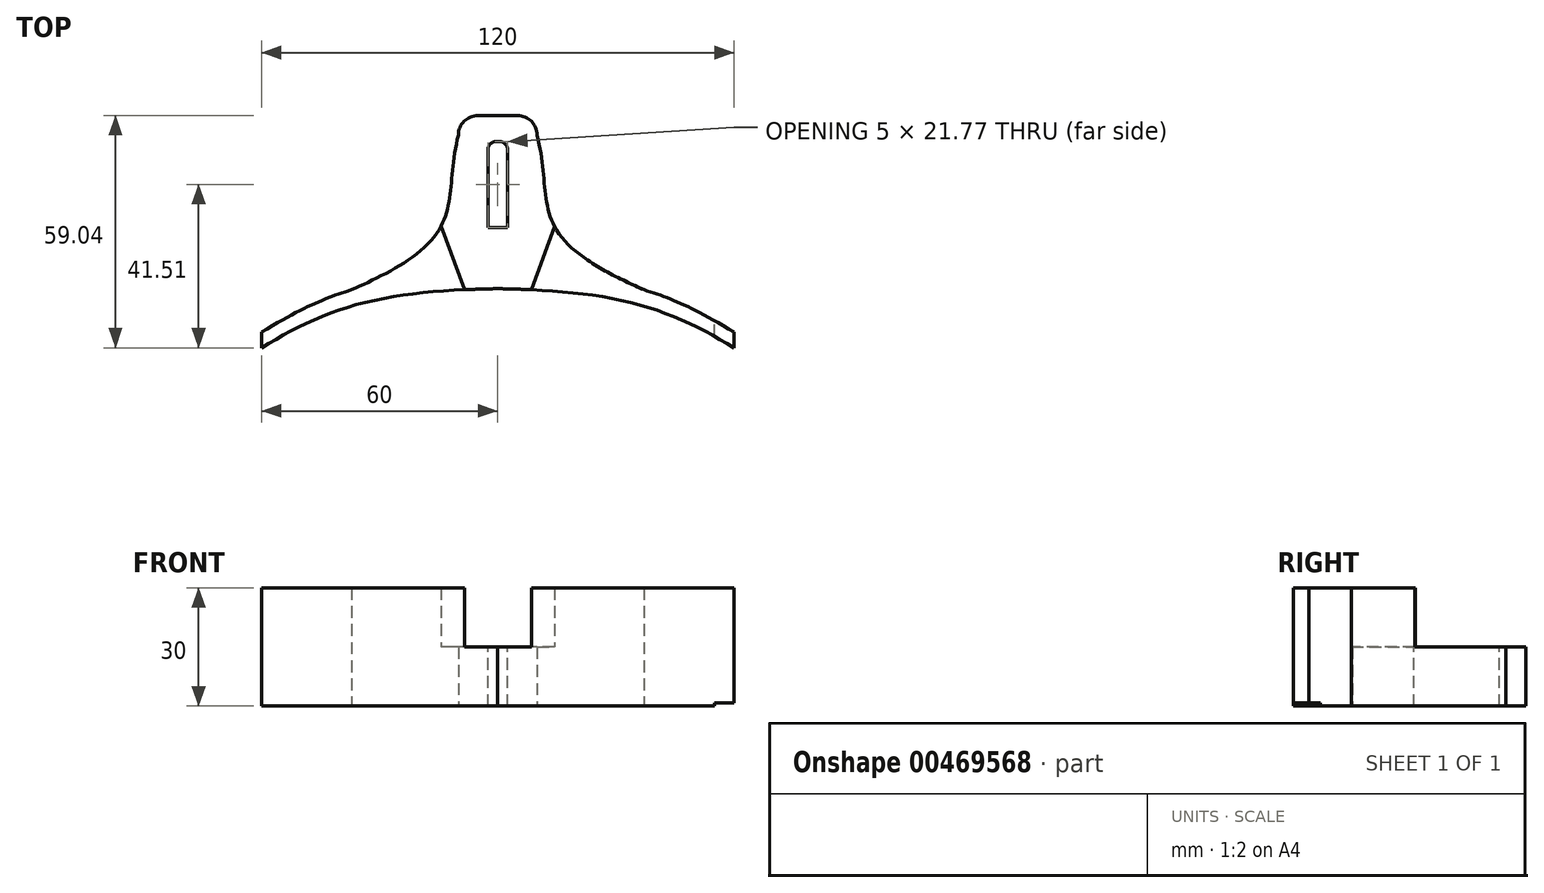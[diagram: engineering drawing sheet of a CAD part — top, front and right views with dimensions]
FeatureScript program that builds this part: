
annotation { "Feature Type Name" : "Feature", "Feature Type Description" : "" }
export const myFeature = defineFeature(function(context is Context, id is Id, definition is map)
    precondition{}
    {
        {
            var Q0;
            Q0=qCreatedBy(makeId("Top.planeOp"),FACE);
            var sketch = newSketch(context, id + "F0", { "sketchPlane" : qUnion([Q0])});
            skFitSpline(sketch, "E0", {"points": [v(10, 0) * mm, v(37.1, -4.27) * mm, v(60, -15.04) * mm], "startDerivative": vector(66.42, 0) * mm, "endDerivative": vector(68.25, -40.78) * mm});
            skLineSegment(sketch, "E1", {"start": v(5, 40) * mm, "end": v(0, 40) * mm});
            skPoint(sketch, "E2.visualSharp", {"position": v(10, 40) * mm});
            skArc(sketch, "E2.filletArc", {"start": v(10, 35) * mm, "mid": v(8.54, 38.54) * mm, "end": v(5, 40) * mm});
            skLineSegment(sketch, "E3", {"start": v(60, -15.04) * mm, "end": v(60, -19.04) * mm});
            skFitSpline(sketch, "E4", {"points": [v(60, -19.04) * mm, v(35.82, -8.06) * mm, v(0, -4) * mm], "startDerivative": vector(-46.55, 29) * mm, "endDerivative": vector(-72.62, 1.28) * mm});
            skFitSpline(sketch, "E5", {"points": [v(10, 35) * mm, v(15.27, 10.37) * mm, v(37.1, -4.27) * mm], "startDerivative": vector(15.22, -59.07) * mm, "endDerivative": vector(39.97, -17.86) * mm});
            skLineSegment(sketch, "E6.MirrorCS", {"start": v(-5, 40) * mm, "end": v(0, 40) * mm});
            skLineSegment(sketch, "E7.MirrorCS", {"start": v(-60, -15.04) * mm, "end": v(-60, -19.04) * mm});
            skArc(sketch, "E8.MirrorCS", {"start": v(-10, 35) * mm, "mid": v(-8.54, 38.54) * mm, "end": v(-5, 40) * mm});
            skFitSpline(sketch, "E9.MirrorCS", {"points": [v(-10, 0) * mm, v(-37.1, -4.27) * mm, v(-60, -15.04) * mm], "startDerivative": vector(-66.42, 0) * mm, "endDerivative": vector(-68.25, -40.78) * mm});
            skFitSpline(sketch, "E10.MirrorCS", {"points": [v(-10, 35) * mm, v(-15.27, 10.37) * mm, v(-37.1, -4.27) * mm], "startDerivative": vector(-15.22, -59.07) * mm, "endDerivative": vector(-39.97, -17.86) * mm});
            skPoint(sketch, "E11.MirrorP", {"position": v(-10, 40) * mm});
            skFitSpline(sketch, "E12.MirrorCS", {"points": [v(-60, -19.04) * mm, v(-35.82, -8.06) * mm, v(0, -4) * mm], "startDerivative": vector(46.55, 29) * mm, "endDerivative": vector(72.62, 1.28) * mm});
            skSolve(sketch);
        }
        {
            var Q0;
            Q0 = qSketchRegion(id + "F0", true);
            extrude(context, id + "F1", {"entities" : qUnion([Q0]), "depth" : 30 * mm});
        }
        {
            var Q0;
            Q0=makeQuery(id+"F1.opExtrude","CAP_FACE",FACE,{"disambiguationData":[OSD([sQuery(id+"F0.wireOp",EDGE,"E0"),sQuery(id+"F0.wireOp",EDGE,"E1"),sQuery(id+"F0.wireOp",EDGE,"E2.filletArc"),sQuery(id+"F0.wireOp",EDGE,"E3"),sQuery(id+"F0.wireOp",EDGE,"E4"),sQuery(id+"F0.wireOp",EDGE,"E5"),sQuery(id+"F0.wireOp",EDGE,"E6.MirrorCS"),sQuery(id+"F0.wireOp",EDGE,"E7.MirrorCS"),sQuery(id+"F0.wireOp",EDGE,"E8.MirrorCS"),sQuery(id+"F0.wireOp",EDGE,"E9.MirrorCS"),sQuery(id+"F0.wireOp",EDGE,"E10.MirrorCS"),sQuery(id+"F0.wireOp",EDGE,"E12.MirrorCS")])],"isStart":false});
            var sketch = newSketch(context, id + "F2", { "sketchPlane" : qUnion([Q0])});
            skLineSegment(sketch, "E13", {"start": v(-15, 40) * mm, "end": v(15, 40) * mm});
            skLineSegment(sketch, "E14", {"start": v(15, 40) * mm, "end": v(15, 13.37) * mm});
            skLineSegment(sketch, "E15", {"start": v(15, 13.37) * mm, "end": v(7.09, -8.37) * mm});
            skLineSegment(sketch, "E16", {"start": v(7.09, -8.37) * mm, "end": v(-6.97, -8.37) * mm});
            skLineSegment(sketch, "E17", {"start": v(-6.97, -8.37) * mm, "end": v(-15, 13.68) * mm});
            skLineSegment(sketch, "E18", {"start": v(-15, 13.68) * mm, "end": v(-15, 40) * mm});
            skSolve(sketch);
        }
        {
            var Q0;
            Q0 = qSketchRegion(id + "F2", true);
            extrude(context, id + "F3", {"entities" : qUnion([Q0]), "operationType" : NewBodyOperationType.REMOVE, "oppositeDirection" : true, "depth" : 15 * mm});
        }
        {
            var Q0;
            Q0=makeQuery(id+"F3.boolean.opBoolean","COPY",FACE,{"derivedFrom":makeQuery(id+"F3.opExtrude","CAP_FACE",FACE,{"disambiguationData":[OSD([sQuery(id+"F2.wireOp",EDGE,"E13"),sQuery(id+"F2.wireOp",EDGE,"E14"),sQuery(id+"F2.wireOp",EDGE,"E15"),sQuery(id+"F2.wireOp",EDGE,"E16"),sQuery(id+"F2.wireOp",EDGE,"E17"),sQuery(id+"F2.wireOp",EDGE,"E18")])],"isStart":false})});
            var sketch = newSketch(context, id + "F4", { "sketchPlane" : qUnion([Q0])});
            skLineSegment(sketch, "E19.bottom", {"start": v(-0.5, 33.36) * mm, "end": v(0.5, 33.36) * mm});
            skLineSegment(sketch, "E19.left", {"start": v(-2.5, 31.36) * mm, "end": v(-2.5, 11.59) * mm});
            skLineSegment(sketch, "E19.right", {"start": v(2.5, 31.36) * mm, "end": v(2.5, 11.59) * mm});
            skPoint(sketch, "E20.visualSharp", {"position": v(2.5, 33.36) * mm});
            skArc(sketch, "E20.filletArc", {"start": v(2.5, 31.36) * mm, "mid": v(1.91, 32.77) * mm, "end": v(0.5, 33.36) * mm});
            skPoint(sketch, "E21.visualSharp", {"position": v(-2.5, 33.36) * mm});
            skArc(sketch, "E21.filletArc", {"start": v(-0.5, 33.36) * mm, "mid": v(-1.91, 32.77) * mm, "end": v(-2.5, 31.36) * mm});
            skLineSegment(sketch, "E22", {"start": v(-2.5, 11.59) * mm, "end": v(2.5, 11.59) * mm});
            skSolve(sketch);
        }
        {
            var Q0;
            Q0 = qSketchRegion(id + "F4", true);
            extrude(context, id + "F5", {"entities" : qUnion([Q0]), "operationType" : NewBodyOperationType.REMOVE, "endBound" : BoundingType.UP_TO_NEXT, "oppositeDirection" : true, "depth" : 8 * mm, "offsetDistance" : 25 * mm});
        }
        {
            var Q0;
            Q0=qCreatedBy(makeId("Front.planeOp"),FACE);
            var sketch = newSketch(context, id + "F6", { "sketchPlane" : qUnion([Q0])});
            skLineSegment(sketch, "E23.bottom", {"start": v(55, 0.82) * mm, "end": v(60, 0.82) * mm});
            skLineSegment(sketch, "E23.top", {"start": v(55, 0) * mm, "end": v(60, 0) * mm});
            skLineSegment(sketch, "E23.left", {"start": v(55, 0.82) * mm, "end": v(55, 0) * mm});
            skLineSegment(sketch, "E23.right", {"start": v(60, 0.82) * mm, "end": v(60, 0) * mm});
            skSolve(sketch);
        }
        {
            var Q0;
            Q0 = qSketchRegion(id + "F6", true);
            extrude(context, id + "F7", {"entities" : qUnion([Q0]), "operationType" : NewBodyOperationType.REMOVE, "endBound" : BoundingType.THROUGH_ALL, "depth" : 25 * mm, "offsetDistance" : 25 * mm});
        }
    });
